# Revit family: Toilet-Elongated-American_Standard-Cadet-3483001.020
name_source: partatom
category: Plumbing Fixtures
units: mm (PartAtom-declared; Revit-internal decimal feet)

## family parameters
Always vertical = No
Cut with Voids When Loaded = No
OmniClass Number = 23.45.05.21.11.11
OmniClass Title = Water Operated Water Closets
Part Type = Normal
Room Calculation Point = No
Round Connector Dimension = Use Radius
Shared = Yes
Work Plane-Based = Yes

## types (1)
- 3483001.020
    4142.600 Tank and tank cover only with tank cover locking device = No
    4142.800 Tank and tank cover only with right hand trip lever = No
    4142.900 Tank complete with right hand trip lever and tank cover locking device = No
    ADA Compliant = Yes
    Assembly Code = D2010110
    Bowl Shape = Elongated
    CEC Compliant = Yes
    CW Connection = Yes
    CWFU = 10
    Cold Water Connection Diameter = 1/4"
    Cold Water Connection Height = 10"
    Cold Water Connection Radius = 1/8"
    Cold Water Connection Width = 6"
    Compliance Certifications = Meets or Exceeds ASME A112.19.2-2008 / CSA B45.1-08 for Vitreous
China Fixtures
    Default Elevation = 0"
    Description = Cadet® Pressure Assist Chair Height Elongated EverClean® Bowl
    Finish = Vitreous China-American Standard-020-White
    Flush Rate = 1.6 gpf (6.0 Lpf) and 1.1 gpf (4.2 Lpf)
    HW Connection = No
    HWFU = 0
    Height = 16 1/2"
    Installation Type = Floor Mounted
    Length = 30 1/4"
    Manufacturer = American Standard
    Material = Vitreous China-American Standard-020-White
    Model = 3483001.020
    Product Documentation Link = https://americanstandard.box.com
    Product Page URL = https://www.americanstandard-us.com
    Seat 5321.110 EverClean with Slow Close snap-off hinges = No
    Seat 5324.019 = No
    Type Comments = For use with both 1.1 gpf/4.2 Lpf and 1.6 gpf/6.0 Lpf tanks
    URL = https://www.americanstandard-us.com
    Vent Connection = No
    WFU = 10
    Warranty Information = 1 Year Limited Warranty
    Waste Connection = Yes
    Waste Connection Diameter = 2 1/8"
    Waste Connection Radius = 1 1/16"
    Width = 14"
    Working Pressure = 25 psi - 80 psi

## geometry (parser evidence)
native form markers: Sweep x1
no freeform markers — native parametric forms only
